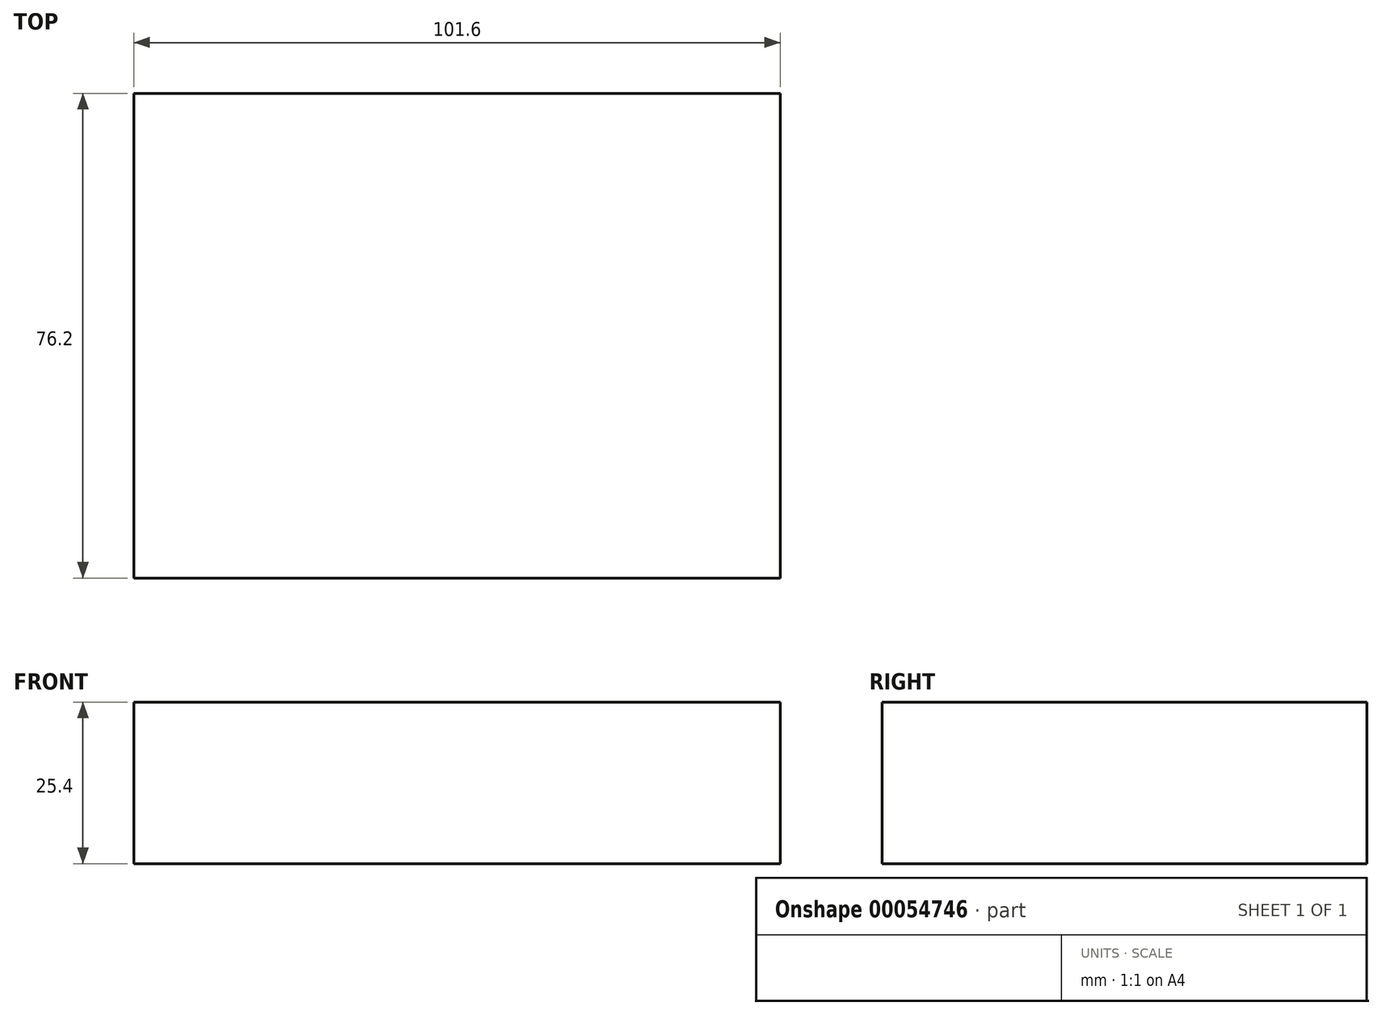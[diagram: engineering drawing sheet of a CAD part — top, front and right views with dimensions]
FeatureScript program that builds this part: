
annotation { "Feature Type Name" : "Feature", "Feature Type Description" : "" }
export const myFeature = defineFeature(function(context is Context, id is Id, definition is map)
    precondition{}
    {
        {
            var Q0;
            Q0=qCreatedBy(makeId("Top.planeOp"),FACE);
            var sketch = newSketch(context, id + "F0", { "sketchPlane" : qUnion([Q0])});
            skLineSegment(sketch, "E0.bottom", {"start": v(-50.8, 38.1) * mm, "end": v(50.8, 38.1) * mm});
            skLineSegment(sketch, "E0.top", {"start": v(-50.8, -38.1) * mm, "end": v(50.8, -38.1) * mm});
            skLineSegment(sketch, "E0.left", {"start": v(-50.8, 38.1) * mm, "end": v(-50.8, -38.1) * mm});
            skLineSegment(sketch, "E0.right", {"start": v(50.8, 38.1) * mm, "end": v(50.8, -38.1) * mm});
            skSolve(sketch);
        }
        {
            var Q0;
            Q0=makeQuery(id+"F0.imprint","IMPRINT",FACE,{"disambiguationData":[TD([[makeQuery(id+"F0.imprint","IMPRINT",EDGE,{"derivedFrom":sQuery(id+"F0.wireOp",EDGE,"E0.bottom")}),-1.0]])]});
            extrude(context, id + "F1", {"entities" : qUnion([Q0]), "depth" : 25.4 * mm});
        }
    });
